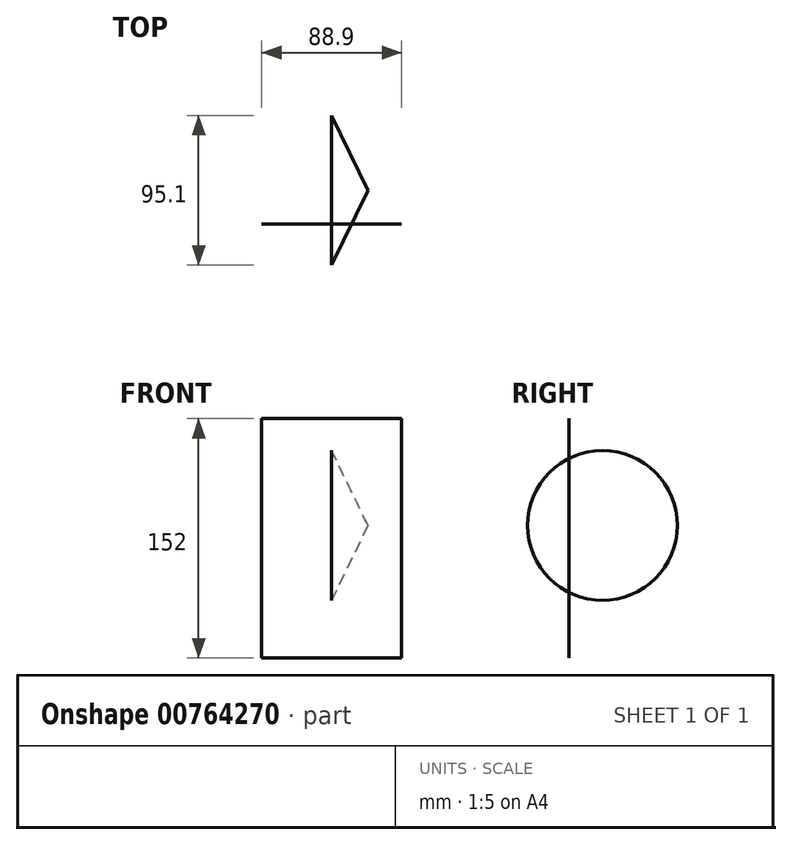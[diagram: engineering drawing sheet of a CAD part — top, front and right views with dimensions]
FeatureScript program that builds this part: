
annotation { "Feature Type Name" : "Feature", "Feature Type Description" : "" }
export const myFeature = defineFeature(function(context is Context, id is Id, definition is map)
    precondition{}
    {
        {
            var Q0;
            Q0=qCreatedBy(makeId("Front.planeOp"),FACE);
            var sketch = newSketch(context, id + "F0", { "sketchPlane" : qUnion([Q0])});
            skLineSegment(sketch, "E0", {"start": v(23.01, 8.5) * mm, "end": v(0, 56.05) * mm});
            skLineSegment(sketch, "E1", {"start": v(23.01, 8.5) * mm, "end": v(0, 8.5) * mm});
            skSolve(sketch);
        }
        {
            var Q0;
            Q0 = qSketchRegion(id + "F0", true);
            var Q1;
            Q1=sQuery(id+"F0.wireOp",EDGE,"E0");
            var Q2;
            Q2=sQuery(id+"F0.wireOp",EDGE,"E1");
            revolve(context, id + "F1", {"bodyType" : ToolBodyType.SURFACE, "surfaceOperationType" : NewSurfaceOperationType.NEW, "entities" : qUnion([Q0]), "surfaceEntities" : qUnion([Q1]), "axis" : qUnion([Q2]), "revolveType" : RevolveType.FULL});
        }
        {
            var Q0;
            Q0=qCreatedBy(makeId("Right.planeOp"),FACE);
            var sketch = newSketch(context, id + "F2", { "sketchPlane" : qUnion([Q0])});
            skLineSegment(sketch, "E2", {"start": v(-21.3, 76.29) * mm, "end": v(-21.3, -75.71) * mm});
            skSolve(sketch);
        }
        {
            var Q0;
            Q0=sQuery(id+"F2.wireOp",EDGE,"E2");
            extrude(context, id + "F3", {"bodyType" : ToolBodyType.SURFACE, "surfaceEntities" : qUnion([Q0]), "endBound" : BoundingType.SYMMETRIC, "depth" : 88.9 * mm, "offsetDistance" : 25.4 * mm});
        }
    });
